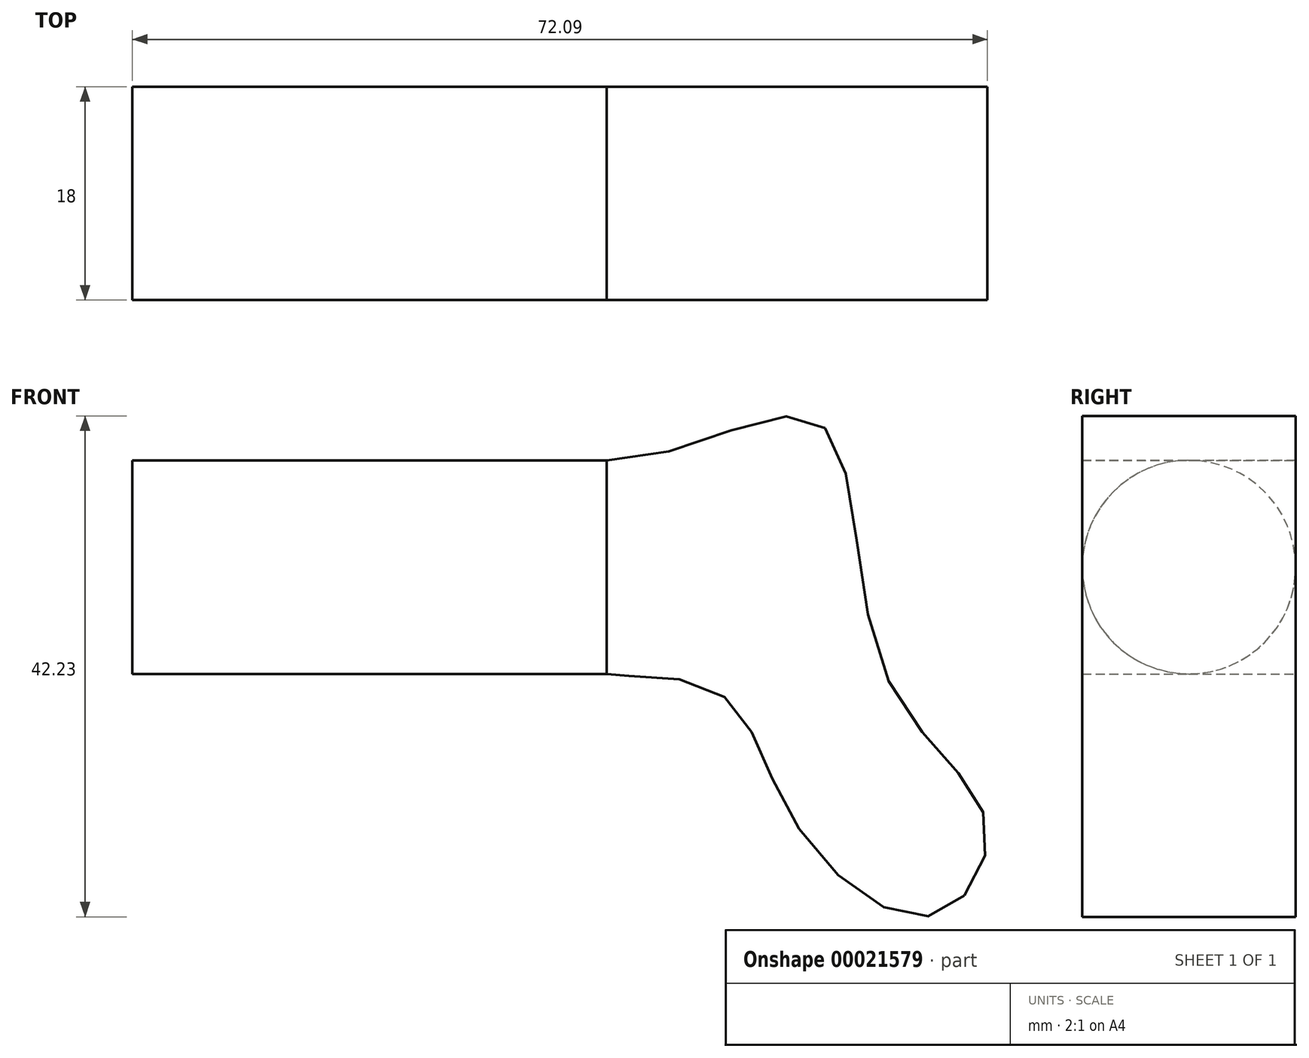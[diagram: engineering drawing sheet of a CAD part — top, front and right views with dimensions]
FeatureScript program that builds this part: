
annotation { "Feature Type Name" : "Feature", "Feature Type Description" : "" }
export const myFeature = defineFeature(function(context is Context, id is Id, definition is map)
    precondition{}
    {
        {
            var Q0;
            Q0=qCreatedBy(makeId("Front.planeOp"),FACE);
            var sketch = newSketch(context, id + "F0", { "sketchPlane" : qUnion([Q0])});
            skLineSegment(sketch, "E0.bottom", {"start": v(0, 0) * mm, "end": v(40, 0) * mm});
            skLineSegment(sketch, "E0.top", {"start": v(0, 9) * mm, "end": v(40, 9) * mm});
            skLineSegment(sketch, "E0.left", {"start": v(0, 0) * mm, "end": v(0, 9) * mm});
            skLineSegment(sketch, "E0.right", {"start": v(40, 0) * mm, "end": v(40, 9) * mm});
            skSolve(sketch);
        }
        {
            var Q0;
            Q0=makeQuery(id+"F0.imprint","IMPRINT",FACE,{"disambiguationData":[TD([[makeQuery(id+"F0.imprint","IMPRINT",EDGE,{"derivedFrom":sQuery(id+"F0.wireOp",EDGE,"E0.bottom")}),1.0]])]});
            var Q1;
            Q1=sQuery(id+"F0.wireOp",EDGE,"E0.bottom");
            revolve(context, id + "F1", {"entities" : qUnion([Q0]), "axis" : qUnion([Q1]), "revolveType" : RevolveType.FULL});
        }
        {
            var Q0;
            Q0=qCreatedBy(makeId("Front.planeOp"),FACE);
            var sketch = newSketch(context, id + "F2", { "sketchPlane" : qUnion([Q0])});
            skLineSegment(sketch, "E1.0", {"start": v(40, 0) * mm, "end": v(40, 9) * mm});
            skFitSpline(sketch, "E2", {"points": [v(40, 9) * mm, v(57.66, 12.3) * mm, v(63.35, -8.72) * mm, v(72, -21.67) * mm, v(67.37, -29.39) * mm, v(55.47, -20.87) * mm, v(48.51, -10.11) * mm, v(40, -9) * mm], "startDerivative": vector(114.38, -7.06) * mm, "endDerivative": vector(6.9, 10.36) * mm});
            skLineSegment(sketch, "E3", {"start": v(40, 0) * mm, "end": v(40, -9) * mm});
            skSolve(sketch);
        }
        {
            var Q0;
            Q0=makeQuery(id+"F2.imprint","IMPRINT",FACE,{"disambiguationData":[TD([[makeQuery(id+"F2.imprint","IMPRINT",EDGE,{"derivedFrom":sQuery(id+"F2.wireOp",EDGE,"E1.0")}),-1.0]])]});
            extrude(context, id + "F3", {"entities" : qUnion([Q0]), "operationType" : NewBodyOperationType.ADD, "depth" : 9 * mm, "hasSecondDirection" : true, "secondDirectionOppositeDirection" : true, "secondDirectionDepth" : 9 * mm});
        }
    });
